# Revit family: Palace_Multi_OXXO_Standard
name_source: partatom
category: Doors
revit_build: Autodesk Revit 2014 (Build: 20130308_1515(x64)
units: mm (PartAtom-declared; Revit-internal decimal feet)

## types (36) — shared parameters
Centered In Wall = Yes
Custom Sash Width Side = 800 mm  [stored 2.62467 ft]
DG Air Gap Thickness = 12 mm  [stored 0.0393701 ft]
DG Thickness Calc = 6 mm  [stored 0.019685 ft]
Description = High performance sliding door, OXXO
Double Glazing Gasket Material = Double Glazing Gasket Material
Equal Sash Width = Yes
Frame Thickness = 118 mm
Limit Door Height Max = 2390 mm  [stored 7.84121 ft]
Limit Door Height Min = 359 mm
Limit Door Width Min = 1188 mm
Limit Sash Height Max = 2400 mm  [stored 7.87402 ft]
Limit Sash Height Min = 300 mm  [stored 0.984252 ft]
Limit Sash Width Max = 1500 mm  [stored 4.92126 ft]
Limit Sash Width Min = 300 mm  [stored 0.984252 ft]
Manufacturer = Crealco
Max System DG One Piece Thickness = 6 mm  [stored 0.019685 ft]
Max System DG Unit Thickness = 25 mm  [stored 0.082021 ft]
Model = Palace
Sash Bottom Gap = 31 mm  [stored 0.101706 ft]
Sash Frame Seal = 3 mm  [stored 0.00984252 ft]
Sash Side Gap = 33 mm  [stored 0.108268 ft]
Sash Sliding Frame Front Back Gap = 10 mm  [stored 0.0328084 ft]
Sash Top Gap = 28 mm  [stored 0.0918635 ft]
URL = http://www.crealco.co.za
Wall Closure = By host
zero-valued in all types: Custom Frame Offset From Exterior, Default Sill Height

## per-type parameters (varying)
- Palace-3021OXXO-1000Pa: Area Middle Sash Glazing=1.21 m²; Area Side Sash Glazing=1.21 m²; Custom Door Height=2090 mm  [stored 6.85696 ft]; Custom Door Width=2990 mm; Custom Windload=1000 mm  [stored 3.28084 ft]; Height=2090 mm  [stored 6.85696 ft]; Interlock Configuration=0 mm  [stored 0 ft]; Intruderprufe Insulated LowE SHGC Value=0.501; Intruderprufe Insulated LowE U Value=3.07; Intruderprufe Insulated SHGC Value=0.553; Intruderprufe Insulated U Value=3.63; Intruderprufe LowE SHGC Value=0.565; Intruderprufe LowE U Value=4.57; Intruderprufe SHGC Value=0.638; Intruderprufe U Value=5.89; Limit Door Width Max=5990 mm  [stored 19.6522 ft]; Limit Sash Width Side Max=1201 mm; Limit Sash Width Side Min=300 mm  [stored 0.984252 ft]; Max Pane Area=1.21 m²; Meeting Stile Configuration=0 mm  [stored 0 ft]; Sash Height=2031 mm; Sash Width Middle=751 mm; Sash Width Sides=751 mm; Toughened Safety SHGC Value=0.68; Toughened Safety U Value=6; Width=2990 mm; Windload Design=1000 mm  [stored 3.28084 ft]
- Palace-3021OXXO-1500Pa: Area Middle Sash Glazing=1.21 m²; Area Side Sash Glazing=1.21 m²; Custom Door Height=2090 mm  [stored 6.85696 ft]; Custom Door Width=2990 mm; Custom Windload=1500 mm  [stored 4.92126 ft]; Height=2090 mm  [stored 6.85696 ft]; Interlock Configuration=1 mm  [stored 0.00328084 ft]; Intruderprufe Insulated LowE SHGC Value=0.501; Intruderprufe Insulated LowE U Value=3.07; Intruderprufe Insulated SHGC Value=0.553; Intruderprufe Insulated U Value=3.63; Intruderprufe LowE SHGC Value=0.565; Intruderprufe LowE U Value=4.57; Intruderprufe SHGC Value=0.638; Intruderprufe U Value=5.89; Limit Door Width Max=5990 mm  [stored 19.6522 ft]; Limit Sash Width Side Max=1201 mm; Limit Sash Width Side Min=300 mm  [stored 0.984252 ft]; Max Pane Area=1.21 m²; Meeting Stile Configuration=1 mm  [stored 0.00328084 ft]; Sash Height=2031 mm; Sash Width Middle=751 mm; Sash Width Sides=751 mm; Toughened Safety SHGC Value=0.68; Toughened Safety U Value=6; Width=2990 mm; Windload Design=1500 mm  [stored 4.92126 ft]
- Palace-3021OXXO-2000Pa: Area Middle Sash Glazing=1.21 m²; Area Side Sash Glazing=1.21 m²; Custom Door Height=2090 mm  [stored 6.85696 ft]; Custom Door Width=2990 mm; Custom Windload=2000 mm  [stored 6.56168 ft]; Height=2090 mm  [stored 6.85696 ft]; Interlock Configuration=1 mm  [stored 0.00328084 ft]; Intruderprufe Insulated LowE SHGC Value=0.501; Intruderprufe Insulated LowE U Value=3.07; Intruderprufe Insulated SHGC Value=0.553; Intruderprufe Insulated U Value=3.63; Intruderprufe LowE SHGC Value=0.565; Intruderprufe LowE U Value=4.57; Intruderprufe SHGC Value=0.638; Intruderprufe U Value=5.89; Limit Door Width Max=5990 mm  [stored 19.6522 ft]; Limit Sash Width Side Max=1201 mm; Limit Sash Width Side Min=300 mm  [stored 0.984252 ft]; Max Pane Area=1.21 m²; Meeting Stile Configuration=1 mm  [stored 0.00328084 ft]; Sash Height=2031 mm; Sash Width Middle=751 mm; Sash Width Sides=751 mm; Toughened Safety SHGC Value=0.68; Toughened Safety U Value=6; Width=2990 mm; Windload Design=2000 mm  [stored 6.56168 ft]
- Palace-3621OXXO-1000Pa: Area Middle Sash Glazing=1.49 m²; Area Side Sash Glazing=1.49 m²; Custom Door Height=2090 mm  [stored 6.85696 ft]; Custom Door Width=3590 mm; Custom Windload=1000 mm  [stored 3.28084 ft]; Height=2090 mm  [stored 6.85696 ft]; Interlock Configuration=0 mm  [stored 0 ft]; Intruderprufe Insulated LowE SHGC Value=0.508; Intruderprufe Insulated LowE U Value=2.99; Intruderprufe Insulated SHGC Value=0.562; Intruderprufe Insulated U Value=3.58; Intruderprufe LowE SHGC Value=0.574; Intruderprufe LowE U Value=4.52; Intruderprufe SHGC Value=0.649; Intruderprufe U Value=5.9; Limit Door Width Max=5990 mm  [stored 19.6522 ft]; Limit Sash Width Side Max=1500 mm  [stored 4.92126 ft]; Limit Sash Width Side Min=301 mm; Max Pane Area=1.49 m²; Meeting Stile Configuration=0 mm  [stored 0 ft]; Sash Height=2031 mm; Sash Width Middle=901 mm; Sash Width Sides=901 mm; Toughened Safety SHGC Value=0.691; Toughened Safety U Value=6.01; Width=3590 mm; Windload Design=1000 mm  [stored 3.28084 ft]
- Palace-3621OXXO-1500Pa: Area Middle Sash Glazing=1.49 m²; Area Side Sash Glazing=1.49 m²; Custom Door Height=2090 mm  [stored 6.85696 ft]; Custom Door Width=3590 mm; Custom Windload=1500 mm  [stored 4.92126 ft]; Height=2090 mm  [stored 6.85696 ft]; Interlock Configuration=1 mm  [stored 0.00328084 ft]; Intruderprufe Insulated LowE SHGC Value=0.508; Intruderprufe Insulated LowE U Value=2.99; Intruderprufe Insulated SHGC Value=0.562; Intruderprufe Insulated U Value=3.58; Intruderprufe LowE SHGC Value=0.574; Intruderprufe LowE U Value=4.52; Intruderprufe SHGC Value=0.649; Intruderprufe U Value=5.9; Limit Door Width Max=5990 mm  [stored 19.6522 ft]; Limit Sash Width Side Max=1500 mm  [stored 4.92126 ft]; Limit Sash Width Side Min=301 mm; Max Pane Area=1.49 m²; Meeting Stile Configuration=1 mm  [stored 0.00328084 ft]; Sash Height=2031 mm; Sash Width Middle=901 mm; Sash Width Sides=901 mm; Toughened Safety SHGC Value=0.691; Toughened Safety U Value=6.01; Width=3590 mm; Windload Design=1500 mm  [stored 4.92126 ft]
- Palace-3621OXXO-2000Pa: Area Middle Sash Glazing=1.49 m²; Area Side Sash Glazing=1.49 m²; Custom Door Height=2090 mm  [stored 6.85696 ft]; Custom Door Width=3590 mm; Custom Windload=2000 mm  [stored 6.56168 ft]; Height=2090 mm  [stored 6.85696 ft]; Interlock Configuration=1 mm  [stored 0.00328084 ft]; Intruderprufe Insulated LowE SHGC Value=0.508; Intruderprufe Insulated LowE U Value=2.99; Intruderprufe Insulated SHGC Value=0.562; Intruderprufe Insulated U Value=3.58; Intruderprufe LowE SHGC Value=0.574; Intruderprufe LowE U Value=4.52; Intruderprufe SHGC Value=0.649; Intruderprufe U Value=5.9; Limit Door Width Max=5990 mm  [stored 19.6522 ft]; Limit Sash Width Side Max=1500 mm  [stored 4.92126 ft]; Limit Sash Width Side Min=301 mm; Max Pane Area=1.49 m²; Meeting Stile Configuration=1 mm  [stored 0.00328084 ft]; Sash Height=2031 mm; Sash Width Middle=901 mm; Sash Width Sides=901 mm; Toughened Safety SHGC Value=0.691; Toughened Safety U Value=6.01; Width=3590 mm; Windload Design=2000 mm  [stored 6.56168 ft]
- Palace-4221OXXO-1000Pa: Area Middle Sash Glazing=1.77 m²; Area Side Sash Glazing=1.77 m²; Custom Door Height=2090 mm  [stored 6.85696 ft]; Custom Door Width=4190 mm; Custom Windload=1000 mm  [stored 3.28084 ft]; Height=2090 mm  [stored 6.85696 ft]; Interlock Configuration=1 mm  [stored 0.00328084 ft]; Intruderprufe Insulated LowE SHGC Value=0.514; Intruderprufe Insulated LowE U Value=2.94; Intruderprufe Insulated SHGC Value=0.569; Intruderprufe Insulated U Value=3.54; Intruderprufe LowE SHGC Value=0.58; Intruderprufe LowE U Value=4.48; Intruderprufe SHGC Value=0.656; Intruderprufe U Value=5.91; Limit Door Width Max=5990 mm  [stored 19.6522 ft]; Limit Sash Width Side Max=1500 mm  [stored 4.92126 ft]; Limit Sash Width Side Min=601 mm; Max Pane Area=1.77 m²; Meeting Stile Configuration=1 mm  [stored 0.00328084 ft]; Sash Height=2031 mm; Sash Width Middle=1051 mm; Sash Width Sides=1051 mm; Toughened Safety SHGC Value=0.699; Toughened Safety U Value=6.02; Width=4190 mm; Windload Design=1000 mm  [stored 3.28084 ft]
- Palace-4221OXXO-1500Pa: Area Middle Sash Glazing=1.77 m²; Area Side Sash Glazing=1.77 m²; Custom Door Height=2090 mm  [stored 6.85696 ft]; Custom Door Width=4190 mm; Custom Windload=1500 mm  [stored 4.92126 ft]; Height=2090 mm  [stored 6.85696 ft]; Interlock Configuration=1 mm  [stored 0.00328084 ft]; Intruderprufe Insulated LowE SHGC Value=0.514; Intruderprufe Insulated LowE U Value=2.94; Intruderprufe Insulated SHGC Value=0.569; Intruderprufe Insulated U Value=3.54; Intruderprufe LowE SHGC Value=0.58; Intruderprufe LowE U Value=4.48; Intruderprufe SHGC Value=0.656; Intruderprufe U Value=5.91; Limit Door Width Max=5990 mm  [stored 19.6522 ft]; Limit Sash Width Side Max=1500 mm  [stored 4.92126 ft]; Limit Sash Width Side Min=601 mm; Max Pane Area=1.77 m²; Meeting Stile Configuration=1 mm  [stored 0.00328084 ft]; Sash Height=2031 mm; Sash Width Middle=1051 mm; Sash Width Sides=1051 mm; Toughened Safety SHGC Value=0.699; Toughened Safety U Value=6.02; Width=4190 mm; Windload Design=1500 mm  [stored 4.92126 ft]
- Palace-4221OXXO-2000Pa: Area Middle Sash Glazing=1.77 m²; Area Side Sash Glazing=1.77 m²; Custom Door Height=2090 mm  [stored 6.85696 ft]; Custom Door Width=4190 mm; Custom Windload=2000 mm  [stored 6.56168 ft]; Height=2090 mm  [stored 6.85696 ft]; Interlock Configuration=1 mm  [stored 0.00328084 ft]; Intruderprufe Insulated LowE SHGC Value=0.514; Intruderprufe Insulated LowE U Value=2.94; Intruderprufe Insulated SHGC Value=0.569; Intruderprufe Insulated U Value=3.54; Intruderprufe LowE SHGC Value=0.58; Intruderprufe LowE U Value=4.48; Intruderprufe SHGC Value=0.656; Intruderprufe U Value=5.91; Limit Door Width Max=5990 mm  [stored 19.6522 ft]; Limit Sash Width Side Max=1500 mm  [stored 4.92126 ft]; Limit Sash Width Side Min=601 mm; Max Pane Area=1.77 m²; Meeting Stile Configuration=1 mm  [stored 0.00328084 ft]; Sash Height=2031 mm; Sash Width Middle=1051 mm; Sash Width Sides=1051 mm; Toughened Safety SHGC Value=0.699; Toughened Safety U Value=6.02; Width=4190 mm; Windload Design=2000 mm  [stored 6.56168 ft]
- Palace-4821OXXO-1000Pa: Area Middle Sash Glazing=2.06 m²; Area Side Sash Glazing=2.06 m²; Custom Door Height=2090 mm  [stored 6.85696 ft]; Custom Door Width=4790 mm  [stored 15.7152 ft]; Custom Windload=1000 mm  [stored 3.28084 ft]; Height=2090 mm  [stored 6.85696 ft]; Interlock Configuration=1 mm  [stored 0.00328084 ft]; Intruderprufe Insulated LowE SHGC Value=0.518; Intruderprufe Insulated LowE U Value=2.9; Intruderprufe Insulated SHGC Value=0.574; Intruderprufe Insulated U Value=3.51; Intruderprufe LowE SHGC Value=0.585; Intruderprufe LowE U Value=4.46; Intruderprufe SHGC Value=0.662; Intruderprufe U Value=5.92; Limit Door Width Max=5990 mm  [stored 19.6522 ft]; Limit Sash Width Side Max=1500 mm  [stored 4.92126 ft]; Limit Sash Width Side Min=901 mm; Max Pane Area=2.06 m²; Meeting Stile Configuration=1 mm  [stored 0.00328084 ft]; Sash Height=2031 mm; Sash Width Middle=1201 mm; Sash Width Sides=1201 mm; Toughened Safety SHGC Value=0.705; Toughened Safety U Value=6.03; Width=4790 mm  [stored 15.7152 ft]; Windload Design=1000 mm  [stored 3.28084 ft]
- Palace-4821OXXO-1500Pa: Area Middle Sash Glazing=2.06 m²; Area Side Sash Glazing=2.06 m²; Custom Door Height=2090 mm  [stored 6.85696 ft]; Custom Door Width=4790 mm  [stored 15.7152 ft]; Custom Windload=1500 mm  [stored 4.92126 ft]; Height=2090 mm  [stored 6.85696 ft]; Interlock Configuration=1 mm  [stored 0.00328084 ft]; Intruderprufe Insulated LowE SHGC Value=0.518; Intruderprufe Insulated LowE U Value=2.9; Intruderprufe Insulated SHGC Value=0.574; Intruderprufe Insulated U Value=3.51; Intruderprufe LowE SHGC Value=0.585; Intruderprufe LowE U Value=4.46; Intruderprufe SHGC Value=0.662; Intruderprufe U Value=5.92; Limit Door Width Max=5990 mm  [stored 19.6522 ft]; Limit Sash Width Side Max=1500 mm  [stored 4.92126 ft]; Limit Sash Width Side Min=901 mm; Max Pane Area=2.06 m²; Meeting Stile Configuration=1 mm  [stored 0.00328084 ft]; Sash Height=2031 mm; Sash Width Middle=1201 mm; Sash Width Sides=1201 mm; Toughened Safety SHGC Value=0.705; Toughened Safety U Value=6.03; Width=4790 mm  [stored 15.7152 ft]; Windload Design=1500 mm  [stored 4.92126 ft]
- Palace-4821OXXO-2000Pa: Area Middle Sash Glazing=2.06 m²; Area Side Sash Glazing=2.06 m²; Custom Door Height=2090 mm  [stored 6.85696 ft]; Custom Door Width=4790 mm  [stored 15.7152 ft]; Custom Windload=2000 mm  [stored 6.56168 ft]; Height=2090 mm  [stored 6.85696 ft]; Interlock Configuration=1 mm  [stored 0.00328084 ft]; Intruderprufe Insulated LowE SHGC Value=0.518; Intruderprufe Insulated LowE U Value=2.9; Intruderprufe Insulated SHGC Value=0.574; Intruderprufe Insulated U Value=3.51; Intruderprufe LowE SHGC Value=0.585; Intruderprufe LowE U Value=4.46; Intruderprufe SHGC Value=0.662; Intruderprufe U Value=5.92; Limit Door Width Max=5990 mm  [stored 19.6522 ft]; Limit Sash Width Side Max=1500 mm  [stored 4.92126 ft]; Limit Sash Width Side Min=901 mm; Max Pane Area=2.06 m²; Meeting Stile Configuration=1 mm  [stored 0.00328084 ft]; Sash Height=2031 mm; Sash Width Middle=1201 mm; Sash Width Sides=1201 mm; Toughened Safety SHGC Value=0.705; Toughened Safety U Value=6.03; Width=4790 mm  [stored 15.7152 ft]; Windload Design=2000 mm  [stored 6.56168 ft]
- Palace-5421OXXO-1000Pa: Area Middle Sash Glazing=2.34 m²; Area Side Sash Glazing=2.34 m²; Custom Door Height=2090 mm  [stored 6.85696 ft]; Custom Door Width=5390 mm; Custom Windload=1000 mm  [stored 3.28084 ft]; Height=2090 mm  [stored 6.85696 ft]; Interlock Configuration=1 mm  [stored 0.00328084 ft]; Intruderprufe Insulated LowE SHGC Value=0.521; Intruderprufe Insulated LowE U Value=2.87; Intruderprufe Insulated SHGC Value=0.577; Intruderprufe Insulated U Value=3.49; Intruderprufe LowE SHGC Value=0.589; Intruderprufe LowE U Value=4.43; Intruderprufe SHGC Value=0.666; Intruderprufe U Value=5.93; Limit Door Width Max=5990 mm  [stored 19.6522 ft]; Limit Sash Width Side Max=1500 mm  [stored 4.92126 ft]; Limit Sash Width Side Min=1201 mm; Max Pane Area=2.34 m²; Meeting Stile Configuration=1 mm  [stored 0.00328084 ft]; Sash Height=2031 mm; Sash Width Middle=1351 mm; Sash Width Sides=1351 mm; Toughened Safety SHGC Value=0.709; Toughened Safety U Value=6.03; Width=5390 mm; Windload Design=1000 mm  [stored 3.28084 ft]
- Palace-5421OXXO-1500Pa: Area Middle Sash Glazing=2.34 m²; Area Side Sash Glazing=2.34 m²; Custom Door Height=2090 mm  [stored 6.85696 ft]; Custom Door Width=5390 mm; Custom Windload=1500 mm  [stored 4.92126 ft]; Height=2090 mm  [stored 6.85696 ft]; Interlock Configuration=1 mm  [stored 0.00328084 ft]; Intruderprufe Insulated LowE SHGC Value=0.521; Intruderprufe Insulated LowE U Value=2.87; Intruderprufe Insulated SHGC Value=0.577; Intruderprufe Insulated U Value=3.49; Intruderprufe LowE SHGC Value=0.589; Intruderprufe LowE U Value=4.43; Intruderprufe SHGC Value=0.666; Intruderprufe U Value=5.93; Limit Door Width Max=5990 mm  [stored 19.6522 ft]; Limit Sash Width Side Max=1500 mm  [stored 4.92126 ft]; Limit Sash Width Side Min=1201 mm; Max Pane Area=2.34 m²; Meeting Stile Configuration=1 mm  [stored 0.00328084 ft]; Sash Height=2031 mm; Sash Width Middle=1351 mm; Sash Width Sides=1351 mm; Toughened Safety SHGC Value=0.709; Toughened Safety U Value=6.03; Width=5390 mm; Windload Design=1500 mm  [stored 4.92126 ft]
- Palace-5421OXXO-2000Pa: Area Middle Sash Glazing=2.34 m²; Area Side Sash Glazing=2.34 m²; Custom Door Height=2090 mm  [stored 6.85696 ft]; Custom Door Width=5390 mm; Custom Windload=2000 mm  [stored 6.56168 ft]; Height=2090 mm  [stored 6.85696 ft]; Interlock Configuration=1 mm  [stored 0.00328084 ft]; Intruderprufe Insulated LowE SHGC Value=0.521; Intruderprufe Insulated LowE U Value=2.87; Intruderprufe Insulated SHGC Value=0.577; Intruderprufe Insulated U Value=3.49; Intruderprufe LowE SHGC Value=0.589; Intruderprufe LowE U Value=4.43; Intruderprufe SHGC Value=0.666; Intruderprufe U Value=5.93; Limit Door Width Max=5990 mm  [stored 19.6522 ft]; Limit Sash Width Side Max=1500 mm  [stored 4.92126 ft]; Limit Sash Width Side Min=1201 mm; Max Pane Area=2.34 m²; Meeting Stile Configuration=1 mm  [stored 0.00328084 ft]; Sash Height=2031 mm; Sash Width Middle=1351 mm; Sash Width Sides=1351 mm; Toughened Safety SHGC Value=0.709; Toughened Safety U Value=6.03; Width=5390 mm; Windload Design=2000 mm  [stored 6.56168 ft]
- Palace-6021OXXO-1000Pa: Area Middle Sash Glazing=2.62 m²; Area Side Sash Glazing=2.62 m²; Custom Door Height=2090 mm  [stored 6.85696 ft]; Custom Door Width=5990 mm  [stored 19.6522 ft]; Custom Windload=1000 mm  [stored 3.28084 ft]; Height=2090 mm  [stored 6.85696 ft]; Interlock Configuration=1 mm  [stored 0.00328084 ft]; Intruderprufe Insulated LowE SHGC Value=0.524; Intruderprufe Insulated LowE U Value=2.85; Intruderprufe Insulated SHGC Value=0.58; Intruderprufe Insulated U Value=3.47; Intruderprufe LowE SHGC Value=0; Intruderprufe LowE U Value=7.9; Intruderprufe SHGC Value=0; Intruderprufe U Value=7.9; Limit Door Width Max=5990 mm  [stored 19.6522 ft]; Limit Sash Width Side Max=1500 mm  [stored 4.92126 ft]; Limit Sash Width Side Min=1501 mm; Max Pane Area=2.62 m²; Meeting Stile Configuration=1 mm  [stored 0.00328084 ft]; Sash Height=2031 mm; Sash Width Middle=1501 mm; Sash Width Sides=1501 mm; Toughened Safety SHGC Value=0.713; Toughened Safety U Value=6.04; Width=5990 mm  [stored 19.6522 ft]; Windload Design=1000 mm  [stored 3.28084 ft]
- Palace-6021OXXO-1500Pa: Area Middle Sash Glazing=2.62 m²; Area Side Sash Glazing=2.62 m²; Custom Door Height=2090 mm  [stored 6.85696 ft]; Custom Door Width=5990 mm  [stored 19.6522 ft]; Custom Windload=1500 mm  [stored 4.92126 ft]; Height=2090 mm  [stored 6.85696 ft]; Interlock Configuration=1 mm  [stored 0.00328084 ft]; Intruderprufe Insulated LowE SHGC Value=0.524; Intruderprufe Insulated LowE U Value=2.85; Intruderprufe Insulated SHGC Value=0.58; Intruderprufe Insulated U Value=3.47; Intruderprufe LowE SHGC Value=0; Intruderprufe LowE U Value=7.9; Intruderprufe SHGC Value=0; Intruderprufe U Value=7.9; Limit Door Width Max=5990 mm  [stored 19.6522 ft]; Limit Sash Width Side Max=1500 mm  [stored 4.92126 ft]; Limit Sash Width Side Min=1501 mm; Max Pane Area=2.62 m²; Meeting Stile Configuration=1 mm  [stored 0.00328084 ft]; Sash Height=2031 mm; Sash Width Middle=1501 mm; Sash Width Sides=1501 mm; Toughened Safety SHGC Value=0.713; Toughened Safety U Value=6.04; Width=5990 mm  [stored 19.6522 ft]; Windload Design=1500 mm  [stored 4.92126 ft]
- Palace-6021OXXO-2000Pa: Area Middle Sash Glazing=2.62 m²; Area Side Sash Glazing=2.62 m²; Custom Door Height=2090 mm  [stored 6.85696 ft]; Custom Door Width=5990 mm  [stored 19.6522 ft]; Custom Windload=2000 mm  [stored 6.56168 ft]; Height=2090 mm  [stored 6.85696 ft]; Interlock Configuration=1 mm  [stored 0.00328084 ft]; Intruderprufe Insulated LowE SHGC Value=0.524; Intruderprufe Insulated LowE U Value=2.85; Intruderprufe Insulated SHGC Value=0.58; Intruderprufe Insulated U Value=3.47; Intruderprufe LowE SHGC Value=0; Intruderprufe LowE U Value=7.9; Intruderprufe SHGC Value=0; Intruderprufe U Value=7.9; Limit Door Width Max=5990 mm  [stored 19.6522 ft]; Limit Sash Width Side Max=1500 mm  [stored 4.92126 ft]; Limit Sash Width Side Min=1501 mm; Max Pane Area=2.62 m²; Meeting Stile Configuration=1 mm  [stored 0.00328084 ft]; Sash Height=2031 mm; Sash Width Middle=1501 mm; Sash Width Sides=1501 mm; Toughened Safety SHGC Value=0.713; Toughened Safety U Value=6.04; Width=5990 mm  [stored 19.6522 ft]; Windload Design=2000 mm  [stored 6.56168 ft]
- Palace-3024OXXO-1000Pa: Area Middle Sash Glazing=1.4 m²; Area Side Sash Glazing=1.4 m²; Custom Door Height=2390 mm  [stored 7.84121 ft]; Custom Door Width=2990 mm; Custom Windload=1000 mm  [stored 3.28084 ft]; Height=2390 mm  [stored 7.84121 ft]; Interlock Configuration=1 mm  [stored 0.00328084 ft]; Intruderprufe Insulated LowE SHGC Value=0.509; Intruderprufe Insulated LowE U Value=2.99; Intruderprufe Insulated SHGC Value=0.563; Intruderprufe Insulated U Value=3.57; Intruderprufe LowE SHGC Value=0.574; Intruderprufe LowE U Value=4.52; Intruderprufe SHGC Value=0.65; Intruderprufe U Value=5.87; Limit Door Width Max=5990 mm  [stored 19.6522 ft]; Limit Sash Width Side Max=1201 mm; Limit Sash Width Side Min=300 mm  [stored 0.984252 ft]; Max Pane Area=1.4 m²; Meeting Stile Configuration=1 mm  [stored 0.00328084 ft]; Sash Height=2331 mm  [stored 7.64764 ft]; Sash Width Middle=751 mm; Sash Width Sides=751 mm; Toughened Safety SHGC Value=0.692; Toughened Safety U Value=5.98; Width=2990 mm; Windload Design=1000 mm  [stored 3.28084 ft]
- Palace-3024OXXO-1500Pa: Area Middle Sash Glazing=1.4 m²; Area Side Sash Glazing=1.4 m²; Custom Door Height=2390 mm  [stored 7.84121 ft]; Custom Door Width=2990 mm; Custom Windload=1500 mm  [stored 4.92126 ft]; Height=2390 mm  [stored 7.84121 ft]; Interlock Configuration=1 mm  [stored 0.00328084 ft]; Intruderprufe Insulated LowE SHGC Value=0.509; Intruderprufe Insulated LowE U Value=2.99; Intruderprufe Insulated SHGC Value=0.563; Intruderprufe Insulated U Value=3.57; Intruderprufe LowE SHGC Value=0.574; Intruderprufe LowE U Value=4.52; Intruderprufe SHGC Value=0.65; Intruderprufe U Value=5.87; Limit Door Width Max=5990 mm  [stored 19.6522 ft]; Limit Sash Width Side Max=1201 mm; Limit Sash Width Side Min=300 mm  [stored 0.984252 ft]; Max Pane Area=1.4 m²; Meeting Stile Configuration=1 mm  [stored 0.00328084 ft]; Sash Height=2331 mm  [stored 7.64764 ft]; Sash Width Middle=751 mm; Sash Width Sides=751 mm; Toughened Safety SHGC Value=0.692; Toughened Safety U Value=5.98; Width=2990 mm; Windload Design=1500 mm  [stored 4.92126 ft]
- Palace-3024OXXO-2000Pa: Area Middle Sash Glazing=1.4 m²; Area Side Sash Glazing=1.4 m²; Custom Door Height=2390 mm  [stored 7.84121 ft]; Custom Door Width=2990 mm; Custom Windload=2000 mm  [stored 6.56168 ft]; Height=2390 mm  [stored 7.84121 ft]; Interlock Configuration=1 mm  [stored 0.00328084 ft]; Intruderprufe Insulated LowE SHGC Value=0.509; Intruderprufe Insulated LowE U Value=2.99; Intruderprufe Insulated SHGC Value=0.563; Intruderprufe Insulated U Value=3.57; Intruderprufe LowE SHGC Value=0.574; Intruderprufe LowE U Value=4.52; Intruderprufe SHGC Value=0.65; Intruderprufe U Value=5.87; Limit Door Width Max=4790 mm  [stored 15.7152 ft]; Limit Sash Width Side Max=1201 mm; Limit Sash Width Side Min=300 mm  [stored 0.984252 ft]; Max Pane Area=1.4 m²; Meeting Stile Configuration=1 mm  [stored 0.00328084 ft]; Sash Height=2331 mm  [stored 7.64764 ft]; Sash Width Middle=751 mm; Sash Width Sides=751 mm; Toughened Safety SHGC Value=0.692; Toughened Safety U Value=5.98; Width=2990 mm; Windload Design=2000 mm  [stored 6.56168 ft]
- Palace-3624OXXO-1000Pa: Area Middle Sash Glazing=1.73 m²; Area Side Sash Glazing=1.73 m²; Custom Door Height=2390 mm  [stored 7.84121 ft]; Custom Door Width=3590 mm; Custom Windload=1000 mm  [stored 3.28084 ft]; Height=2390 mm  [stored 7.84121 ft]; Interlock Configuration=1 mm  [stored 0.00328084 ft]; Intruderprufe Insulated LowE SHGC Value=0.517; Intruderprufe Insulated LowE U Value=2.92; Intruderprufe Insulated SHGC Value=0.572; Intruderprufe Insulated U Value=3.51; Intruderprufe LowE SHGC Value=0.584; Intruderprufe LowE U Value=4.46; Intruderprufe SHGC Value=0.66; Intruderprufe U Value=5.89; Limit Door Width Max=5990 mm  [stored 19.6522 ft]; Limit Sash Width Side Max=1500 mm  [stored 4.92126 ft]; Limit Sash Width Side Min=301 mm; Max Pane Area=1.73 m²; Meeting Stile Configuration=1 mm  [stored 0.00328084 ft]; Sash Height=2331 mm  [stored 7.64764 ft]; Sash Width Middle=901 mm; Sash Width Sides=901 mm; Toughened Safety SHGC Value=0.703; Toughened Safety U Value=5.99; Width=3590 mm; Windload Design=1000 mm  [stored 3.28084 ft]
- Palace-3624OXXO-1500Pa: Area Middle Sash Glazing=1.73 m²; Area Side Sash Glazing=1.73 m²; Custom Door Height=2390 mm  [stored 7.84121 ft]; Custom Door Width=3590 mm; Custom Windload=1500 mm  [stored 4.92126 ft]; Height=2390 mm  [stored 7.84121 ft]; Interlock Configuration=1 mm  [stored 0.00328084 ft]; Intruderprufe Insulated LowE SHGC Value=0.517; Intruderprufe Insulated LowE U Value=2.92; Intruderprufe Insulated SHGC Value=0.572; Intruderprufe Insulated U Value=3.51; Intruderprufe LowE SHGC Value=0.584; Intruderprufe LowE U Value=4.46; Intruderprufe SHGC Value=0.66; Intruderprufe U Value=5.89; Limit Door Width Max=5990 mm  [stored 19.6522 ft]; Limit Sash Width Side Max=1500 mm  [stored 4.92126 ft]; Limit Sash Width Side Min=301 mm; Max Pane Area=1.73 m²; Meeting Stile Configuration=1 mm  [stored 0.00328084 ft]; Sash Height=2331 mm  [stored 7.64764 ft]; Sash Width Middle=901 mm; Sash Width Sides=901 mm; Toughened Safety SHGC Value=0.703; Toughened Safety U Value=5.99; Width=3590 mm; Windload Design=1500 mm  [stored 4.92126 ft]
- Palace-3624OXXO-2000Pa: Area Middle Sash Glazing=1.73 m²; Area Side Sash Glazing=1.73 m²; Custom Door Height=2390 mm  [stored 7.84121 ft]; Custom Door Width=3590 mm; Custom Windload=2000 mm  [stored 6.56168 ft]; Height=2390 mm  [stored 7.84121 ft]; Interlock Configuration=1 mm  [stored 0.00328084 ft]; Intruderprufe Insulated LowE SHGC Value=0.517; Intruderprufe Insulated LowE U Value=2.92; Intruderprufe Insulated SHGC Value=0.572; Intruderprufe Insulated U Value=3.51; Intruderprufe LowE SHGC Value=0.584; Intruderprufe LowE U Value=4.46; Intruderprufe SHGC Value=0.66; Intruderprufe U Value=5.89; Limit Door Width Max=4790 mm  [stored 15.7152 ft]; Limit Sash Width Side Max=1500 mm  [stored 4.92126 ft]; Limit Sash Width Side Min=301 mm; Max Pane Area=1.73 m²; Meeting Stile Configuration=1 mm  [stored 0.00328084 ft]; Sash Height=2331 mm  [stored 7.64764 ft]; Sash Width Middle=901 mm; Sash Width Sides=901 mm; Toughened Safety SHGC Value=0.703; Toughened Safety U Value=5.99; Width=3590 mm; Windload Design=2000 mm  [stored 6.56168 ft]
- Palace-4224OXXO-1000Pa: Area Middle Sash Glazing=2.06 m²; Area Side Sash Glazing=2.06 m²; Custom Door Height=2390 mm  [stored 7.84121 ft]; Custom Door Width=4190 mm; Custom Windload=1000 mm  [stored 3.28084 ft]; Height=2390 mm  [stored 7.84121 ft]; Interlock Configuration=1 mm  [stored 0.00328084 ft]; Intruderprufe Insulated LowE SHGC Value=0.523; Intruderprufe Insulated LowE U Value=2.86; Intruderprufe Insulated SHGC Value=0.579; Intruderprufe Insulated U Value=3.47; Intruderprufe LowE SHGC Value=0.59; Intruderprufe LowE U Value=4.42; Intruderprufe SHGC Value=0.668; Intruderprufe U Value=5.89; Limit Door Width Max=5990 mm  [stored 19.6522 ft]; Limit Sash Width Side Max=1500 mm  [stored 4.92126 ft]; Limit Sash Width Side Min=601 mm; Max Pane Area=2.06 m²; Meeting Stile Configuration=1 mm  [stored 0.00328084 ft]; Sash Height=2331 mm  [stored 7.64764 ft]; Sash Width Middle=1051 mm; Sash Width Sides=1051 mm; Toughened Safety SHGC Value=0.711; Toughened Safety U Value=6; Width=4190 mm; Windload Design=1000 mm  [stored 3.28084 ft]
- Palace-4224OXXO-1500Pa: Area Middle Sash Glazing=2.06 m²; Area Side Sash Glazing=2.06 m²; Custom Door Height=2390 mm  [stored 7.84121 ft]; Custom Door Width=4190 mm; Custom Windload=1500 mm  [stored 4.92126 ft]; Height=2390 mm  [stored 7.84121 ft]; Interlock Configuration=1 mm  [stored 0.00328084 ft]; Intruderprufe Insulated LowE SHGC Value=0.523; Intruderprufe Insulated LowE U Value=2.86; Intruderprufe Insulated SHGC Value=0.579; Intruderprufe Insulated U Value=3.47; Intruderprufe LowE SHGC Value=0.59; Intruderprufe LowE U Value=4.42; Intruderprufe SHGC Value=0.668; Intruderprufe U Value=5.89; Limit Door Width Max=5990 mm  [stored 19.6522 ft]; Limit Sash Width Side Max=1500 mm  [stored 4.92126 ft]; Limit Sash Width Side Min=601 mm; Max Pane Area=2.06 m²; Meeting Stile Configuration=1 mm  [stored 0.00328084 ft]; Sash Height=2331 mm  [stored 7.64764 ft]; Sash Width Middle=1051 mm; Sash Width Sides=1051 mm; Toughened Safety SHGC Value=0.711; Toughened Safety U Value=6; Width=4190 mm; Windload Design=1500 mm  [stored 4.92126 ft]
- Palace-4224OXXO-2000Pa: Area Middle Sash Glazing=2.06 m²; Area Side Sash Glazing=2.06 m²; Custom Door Height=2390 mm  [stored 7.84121 ft]; Custom Door Width=4190 mm; Custom Windload=2000 mm  [stored 6.56168 ft]; Height=2390 mm  [stored 7.84121 ft]; Interlock Configuration=1 mm  [stored 0.00328084 ft]; Intruderprufe Insulated LowE SHGC Value=0.523; Intruderprufe Insulated LowE U Value=2.86; Intruderprufe Insulated SHGC Value=0.579; Intruderprufe Insulated U Value=3.47; Intruderprufe LowE SHGC Value=0.59; Intruderprufe LowE U Value=4.42; Intruderprufe SHGC Value=0.668; Intruderprufe U Value=5.89; Limit Door Width Max=4790 mm  [stored 15.7152 ft]; Limit Sash Width Side Max=1500 mm  [stored 4.92126 ft]; Limit Sash Width Side Min=601 mm; Max Pane Area=2.06 m²; Meeting Stile Configuration=1 mm  [stored 0.00328084 ft]; Sash Height=2331 mm  [stored 7.64764 ft]; Sash Width Middle=1051 mm; Sash Width Sides=1051 mm; Toughened Safety SHGC Value=0.711; Toughened Safety U Value=6; Width=4190 mm; Windload Design=2000 mm  [stored 6.56168 ft]
- Palace-4824OXXO-1000Pa: Area Middle Sash Glazing=2.38 m²; Area Side Sash Glazing=2.38 m²; Custom Door Height=2390 mm  [stored 7.84121 ft]; Custom Door Width=4790 mm  [stored 15.7152 ft]; Custom Windload=1000 mm  [stored 3.28084 ft]; Height=2390 mm  [stored 7.84121 ft]; Interlock Configuration=1 mm  [stored 0.00328084 ft]; Intruderprufe Insulated LowE SHGC Value=0.527; Intruderprufe Insulated LowE U Value=2.82; Intruderprufe Insulated SHGC Value=0.584; Intruderprufe Insulated U Value=3.44; Intruderprufe LowE SHGC Value=0.595; Intruderprufe LowE U Value=4.39; Intruderprufe SHGC Value=0.674; Intruderprufe U Value=5.9; Limit Door Width Max=5990 mm  [stored 19.6522 ft]; Limit Sash Width Side Max=1500 mm  [stored 4.92126 ft]; Limit Sash Width Side Min=901 mm; Max Pane Area=2.38 m²; Meeting Stile Configuration=1 mm  [stored 0.00328084 ft]; Sash Height=2331 mm  [stored 7.64764 ft]; Sash Width Middle=1201 mm; Sash Width Sides=1201 mm; Toughened Safety SHGC Value=0.717; Toughened Safety U Value=6.01; Width=4790 mm  [stored 15.7152 ft]; Windload Design=1000 mm  [stored 3.28084 ft]
- Palace-4824OXXO-1500Pa: Area Middle Sash Glazing=2.38 m²; Area Side Sash Glazing=2.38 m²; Custom Door Height=2390 mm  [stored 7.84121 ft]; Custom Door Width=4790 mm  [stored 15.7152 ft]; Custom Windload=1500 mm  [stored 4.92126 ft]; Height=2390 mm  [stored 7.84121 ft]; Interlock Configuration=1 mm  [stored 0.00328084 ft]; Intruderprufe Insulated LowE SHGC Value=0.527; Intruderprufe Insulated LowE U Value=2.82; Intruderprufe Insulated SHGC Value=0.584; Intruderprufe Insulated U Value=3.44; Intruderprufe LowE SHGC Value=0.595; Intruderprufe LowE U Value=4.39; Intruderprufe SHGC Value=0.674; Intruderprufe U Value=5.9; Limit Door Width Max=5990 mm  [stored 19.6522 ft]; Limit Sash Width Side Max=1500 mm  [stored 4.92126 ft]; Limit Sash Width Side Min=901 mm; Max Pane Area=2.38 m²; Meeting Stile Configuration=1 mm  [stored 0.00328084 ft]; Sash Height=2331 mm  [stored 7.64764 ft]; Sash Width Middle=1201 mm; Sash Width Sides=1201 mm; Toughened Safety SHGC Value=0.717; Toughened Safety U Value=6.01; Width=4790 mm  [stored 15.7152 ft]; Windload Design=1500 mm  [stored 4.92126 ft]
- Palace-4824OXXO-2000Pa: Area Middle Sash Glazing=2.38 m²; Area Side Sash Glazing=2.38 m²; Custom Door Height=2390 mm  [stored 7.84121 ft]; Custom Door Width=4790 mm  [stored 15.7152 ft]; Custom Windload=2000 mm  [stored 6.56168 ft]; Height=2390 mm  [stored 7.84121 ft]; Interlock Configuration=1 mm  [stored 0.00328084 ft]; Intruderprufe Insulated LowE SHGC Value=0.527; Intruderprufe Insulated LowE U Value=2.82; Intruderprufe Insulated SHGC Value=0.584; Intruderprufe Insulated U Value=3.44; Intruderprufe LowE SHGC Value=0.595; Intruderprufe LowE U Value=4.39; Intruderprufe SHGC Value=0.674; Intruderprufe U Value=5.9; Limit Door Width Max=4790 mm  [stored 15.7152 ft]; Limit Sash Width Side Max=1500 mm  [stored 4.92126 ft]; Limit Sash Width Side Min=901 mm; Max Pane Area=2.38 m²; Meeting Stile Configuration=1 mm  [stored 0.00328084 ft]; Sash Height=2331 mm  [stored 7.64764 ft]; Sash Width Middle=1201 mm; Sash Width Sides=1201 mm; Toughened Safety SHGC Value=0.717; Toughened Safety U Value=6.01; Width=4790 mm  [stored 15.7152 ft]; Windload Design=2000 mm  [stored 6.56168 ft]
- Palace-5424OXXO-1000Pa: Area Middle Sash Glazing=2.71 m²; Area Side Sash Glazing=2.71 m²; Custom Door Height=2390 mm  [stored 7.84121 ft]; Custom Door Width=5390 mm; Custom Windload=1000 mm  [stored 3.28084 ft]; Height=2390 mm  [stored 7.84121 ft]; Interlock Configuration=1 mm  [stored 0.00328084 ft]; Intruderprufe Insulated LowE SHGC Value=0.53; Intruderprufe Insulated LowE U Value=2.79; Intruderprufe Insulated SHGC Value=0.587; Intruderprufe Insulated U Value=3.42; Intruderprufe LowE SHGC Value=0; Intruderprufe LowE U Value=7.9; Intruderprufe SHGC Value=0; Intruderprufe U Value=7.9; Limit Door Width Max=5990 mm  [stored 19.6522 ft]; Limit Sash Width Side Max=1500 mm  [stored 4.92126 ft]; Limit Sash Width Side Min=1201 mm; Max Pane Area=2.71 m²; Meeting Stile Configuration=1 mm  [stored 0.00328084 ft]; Sash Height=2331 mm  [stored 7.64764 ft]; Sash Width Middle=1351 mm; Sash Width Sides=1351 mm; Toughened Safety SHGC Value=0.722; Toughened Safety U Value=0.601; Width=5390 mm; Windload Design=1000 mm  [stored 3.28084 ft]
- Palace-5424OXXO-1500Pa: Area Middle Sash Glazing=2.71 m²; Area Side Sash Glazing=2.71 m²; Custom Door Height=2390 mm  [stored 7.84121 ft]; Custom Door Width=5390 mm; Custom Windload=1500 mm  [stored 4.92126 ft]; Height=2390 mm  [stored 7.84121 ft]; Interlock Configuration=1 mm  [stored 0.00328084 ft]; Intruderprufe Insulated LowE SHGC Value=0.53; Intruderprufe Insulated LowE U Value=2.79; Intruderprufe Insulated SHGC Value=0.587; Intruderprufe Insulated U Value=3.42; Intruderprufe LowE SHGC Value=0; Intruderprufe LowE U Value=7.9; Intruderprufe SHGC Value=0; Intruderprufe U Value=7.9; Limit Door Width Max=5990 mm  [stored 19.6522 ft]; Limit Sash Width Side Max=1500 mm  [stored 4.92126 ft]; Limit Sash Width Side Min=1201 mm; Max Pane Area=2.71 m²; Meeting Stile Configuration=1 mm  [stored 0.00328084 ft]; Sash Height=2331 mm  [stored 7.64764 ft]; Sash Width Middle=1351 mm; Sash Width Sides=1351 mm; Toughened Safety SHGC Value=0.722; Toughened Safety U Value=0.601; Width=5390 mm; Windload Design=1500 mm  [stored 4.92126 ft]
- Palace-5424OXXO-2000Pa: Area Middle Sash Glazing=2.38 m²; Area Side Sash Glazing=2.38 m²; Custom Door Height=2390 mm  [stored 7.84121 ft]; Custom Door Width=5390 mm; Custom Windload=2000 mm  [stored 6.56168 ft]; Height=2390 mm  [stored 7.84121 ft]; Interlock Configuration=1 mm  [stored 0.00328084 ft]; Intruderprufe Insulated LowE SHGC Value=0.53; Intruderprufe Insulated LowE U Value=2.79; Intruderprufe Insulated SHGC Value=0.587; Intruderprufe Insulated U Value=3.42; Intruderprufe LowE SHGC Value=0; Intruderprufe LowE U Value=7.9; Intruderprufe SHGC Value=0; Intruderprufe U Value=7.9; Limit Door Width Max=4790 mm  [stored 15.7152 ft]; Limit Sash Width Side Max=1500 mm  [stored 4.92126 ft]; Limit Sash Width Side Min=901 mm; Max Pane Area=2.38 m²; Meeting Stile Configuration=1 mm  [stored 0.00328084 ft]; Sash Height=2331 mm  [stored 7.64764 ft]; Sash Width Middle=1201 mm; Sash Width Sides=1201 mm; Toughened Safety SHGC Value=0.722; Toughened Safety U Value=0.601; Width=4790 mm  [stored 15.7152 ft]; Windload Design=2000 mm  [stored 6.56168 ft]
- Palace-6024OXXO-1000Pa: Area Middle Sash Glazing=3.04 m²; Area Side Sash Glazing=3.04 m²; Custom Door Height=2390 mm  [stored 7.84121 ft]; Custom Door Width=5990 mm  [stored 19.6522 ft]; Custom Windload=1000 mm  [stored 3.28084 ft]; Height=2390 mm  [stored 7.84121 ft]; Interlock Configuration=1 mm  [stored 0.00328084 ft]; Intruderprufe Insulated LowE SHGC Value=0.533; Intruderprufe Insulated LowE U Value=2.77; Intruderprufe Insulated SHGC Value=0.59; Intruderprufe Insulated U Value=3.4; Intruderprufe LowE SHGC Value=0; Intruderprufe LowE U Value=7.9; Intruderprufe SHGC Value=0; Intruderprufe U Value=7.9; Limit Door Width Max=5990 mm  [stored 19.6522 ft]; Limit Sash Width Side Max=1500 mm  [stored 4.92126 ft]; Limit Sash Width Side Min=1501 mm; Max Pane Area=3.04 m²; Meeting Stile Configuration=1 mm  [stored 0.00328084 ft]; Sash Height=2331 mm  [stored 7.64764 ft]; Sash Width Middle=1501 mm; Sash Width Sides=1501 mm; Toughened Safety SHGC Value=0.725; Toughened Safety U Value=6.02; Width=5990 mm  [stored 19.6522 ft]; Windload Design=1000 mm  [stored 3.28084 ft]
- Palace-6024OXXO-1500Pa: Area Middle Sash Glazing=3.04 m²; Area Side Sash Glazing=3.04 m²; Custom Door Height=2390 mm  [stored 7.84121 ft]; Custom Door Width=5990 mm  [stored 19.6522 ft]; Custom Windload=1500 mm  [stored 4.92126 ft]; Height=2390 mm  [stored 7.84121 ft]; Interlock Configuration=1 mm  [stored 0.00328084 ft]; Intruderprufe Insulated LowE SHGC Value=0.533; Intruderprufe Insulated LowE U Value=2.77; Intruderprufe Insulated SHGC Value=0.59; Intruderprufe Insulated U Value=3.4; Intruderprufe LowE SHGC Value=0; Intruderprufe LowE U Value=7.9; Intruderprufe SHGC Value=0; Intruderprufe U Value=7.9; Limit Door Width Max=5990 mm  [stored 19.6522 ft]; Limit Sash Width Side Max=1500 mm  [stored 4.92126 ft]; Limit Sash Width Side Min=1501 mm; Max Pane Area=3.04 m²; Meeting Stile Configuration=1 mm  [stored 0.00328084 ft]; Sash Height=2331 mm  [stored 7.64764 ft]; Sash Width Middle=1501 mm; Sash Width Sides=1501 mm; Toughened Safety SHGC Value=0.725; Toughened Safety U Value=6.02; Width=5990 mm  [stored 19.6522 ft]; Windload Design=1500 mm  [stored 4.92126 ft]
- Palace-6024OXXO-2000Pa: Area Middle Sash Glazing=2.38 m²; Area Side Sash Glazing=2.38 m²; Custom Door Height=2390 mm  [stored 7.84121 ft]; Custom Door Width=5990 mm  [stored 19.6522 ft]; Custom Windload=2000 mm  [stored 6.56168 ft]; Height=2390 mm  [stored 7.84121 ft]; Interlock Configuration=1 mm  [stored 0.00328084 ft]; Intruderprufe Insulated LowE SHGC Value=0.533; Intruderprufe Insulated LowE U Value=2.77; Intruderprufe Insulated SHGC Value=0.59; Intruderprufe Insulated U Value=3.4; Intruderprufe LowE SHGC Value=0; Intruderprufe LowE U Value=7.9; Intruderprufe SHGC Value=0; Intruderprufe U Value=7.9; Limit Door Width Max=4790 mm  [stored 15.7152 ft]; Limit Sash Width Side Max=1500 mm  [stored 4.92126 ft]; Limit Sash Width Side Min=901 mm; Max Pane Area=2.38 m²; Meeting Stile Configuration=1 mm  [stored 0.00328084 ft]; Sash Height=2331 mm  [stored 7.64764 ft]; Sash Width Middle=1201 mm; Sash Width Sides=1201 mm; Toughened Safety SHGC Value=0.725; Toughened Safety U Value=6.02; Width=4790 mm  [stored 15.7152 ft]; Windload Design=2000 mm  [stored 6.56168 ft]

note: [stored X ft] marks values corroborated as IEEE doubles in the binary element streams (Revit-internal decimal feet)

## geometry (parser evidence)
native form markers: Sweep x66
no freeform markers — native parametric forms only
